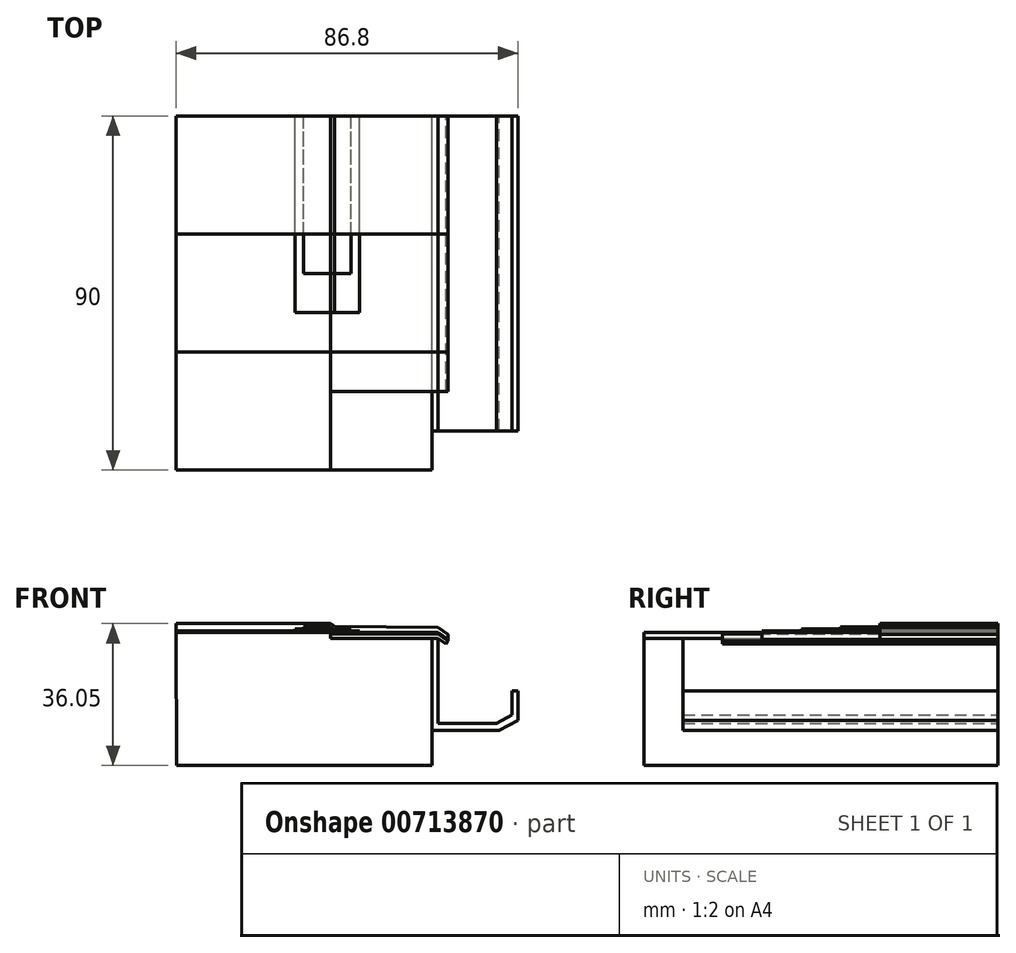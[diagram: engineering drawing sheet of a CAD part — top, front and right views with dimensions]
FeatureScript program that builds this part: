
annotation { "Feature Type Name" : "Feature", "Feature Type Description" : "" }
export const myFeature = defineFeature(function(context is Context, id is Id, definition is map)
    precondition{}
    {
        {
            var Q0;
            Q0=qCreatedBy(makeId("Front.planeOp"),FACE);
            var sketch = newSketch(context, id + "F0", { "sketchPlane" : qUnion([Q0])});
            skLineSegment(sketch, "E0", {"start": v(-75.03, 19.01) * mm, "end": v(-35.84, 19.01) * mm});
            skLineSegment(sketch, "E1", {"start": v(-10, 16.28) * mm, "end": v(-10, -14.78) * mm});
            skLineSegment(sketch, "E2", {"start": v(-10, -14.78) * mm, "end": v(-74.97, -14.78) * mm});
            skLineSegment(sketch, "E3", {"start": v(-74.97, -14.78) * mm, "end": v(-75.03, 19.01) * mm});
            skLineSegment(sketch, "E4", {"start": v(-10, -5.84) * mm, "end": v(7, -5.84) * mm});
            skLineSegment(sketch, "E5", {"start": v(7, -5.84) * mm, "end": v(11.77, -3.36) * mm});
            skLineSegment(sketch, "E6", {"start": v(11.77, -3.36) * mm, "end": v(11.77, 4.25) * mm});
            skLineSegment(sketch, "E7", {"start": v(-35.84, 17.55) * mm, "end": v(-8.56, 17.55) * mm});
            skLineSegment(sketch, "E8", {"start": v(-8.56, 17.55) * mm, "end": v(-8.56, -4.04) * mm});
            skLineSegment(sketch, "E9", {"start": v(-8.56, -4.04) * mm, "end": v(6.35, -4.04) * mm});
            skLineSegment(sketch, "E10", {"start": v(6.35, -4.04) * mm, "end": v(10.35, -1.92) * mm});
            skLineSegment(sketch, "E11", {"start": v(10.35, -1.92) * mm, "end": v(10.35, 4.2) * mm});
            skLineSegment(sketch, "E12", {"start": v(10.35, 4.2) * mm, "end": v(11.77, 4.25) * mm});
            skLineSegment(sketch, "E13", {"start": v(-8.56, 17.55) * mm, "end": v(-6.47, 16.15) * mm});
            skLineSegment(sketch, "E14", {"start": v(-6.47, 16.15) * mm, "end": v(-5.95, 16.94) * mm});
            skLineSegment(sketch, "E15", {"start": v(-5.95, 16.94) * mm, "end": v(-8.56, 18.69) * mm});
            skLineSegment(sketch, "E16", {"start": v(-8.56, 18.69) * mm, "end": v(-35.84, 18.69) * mm});
            skLineSegment(sketch, "E17", {"start": v(-75.03, 19.01) * mm, "end": v(-75.03, 19.4) * mm});
            skLineSegment(sketch, "E18", {"start": v(-75.03, 19.4) * mm, "end": v(-35.84, 19.4) * mm});
            skLineSegment(sketch, "E19", {"start": v(-35.84, 19.4) * mm, "end": v(-35.84, 19.01) * mm});
            skLineSegment(sketch, "E20", {"start": v(-35.84, 19.01) * mm, "end": v(-8.48, 19.01) * mm});
            skLineSegment(sketch, "E21", {"start": v(-8.48, 19.01) * mm, "end": v(-5.95, 17.32) * mm});
            skLineSegment(sketch, "E22", {"start": v(-5.95, 17.32) * mm, "end": v(-5.95, 16.94) * mm});
            skLineSegment(sketch, "E23", {"start": v(-44.83, 19.4) * mm, "end": v(-44.83, 19.98) * mm});
            skLineSegment(sketch, "E24", {"start": v(-44.83, 19.98) * mm, "end": v(-35.84, 19.98) * mm});
            skLineSegment(sketch, "E25", {"start": v(-35.84, 19.98) * mm, "end": v(-34.74, 19.4) * mm});
            skLineSegment(sketch, "E26", {"start": v(-34.74, 19.4) * mm, "end": v(-28.5, 19.4) * mm});
            skLineSegment(sketch, "E27", {"start": v(-28.5, 19.4) * mm, "end": v(-28.5, 19.01) * mm});
            skLineSegment(sketch, "E28", {"start": v(-42.7, 19.98) * mm, "end": v(-42.7, 20.43) * mm});
            skLineSegment(sketch, "E29", {"start": v(-42.7, 20.43) * mm, "end": v(-35.84, 20.43) * mm});
            skLineSegment(sketch, "E30", {"start": v(-35.84, 20.43) * mm, "end": v(-34.79, 19.72) * mm});
            skLineSegment(sketch, "E31", {"start": v(-34.79, 19.72) * mm, "end": v(-30.54, 19.72) * mm});
            skLineSegment(sketch, "E32", {"start": v(-30.54, 19.72) * mm, "end": v(-30.54, 19.4) * mm});
            skLineSegment(sketch, "E33", {"start": v(-75.03, 19.4) * mm, "end": v(-75.03, 21.27) * mm});
            skLineSegment(sketch, "E34", {"start": v(-75.03, 21.27) * mm, "end": v(-35.84, 21.27) * mm});
            skLineSegment(sketch, "E35", {"start": v(-35.84, 21.27) * mm, "end": v(-34.76, 20.54) * mm});
            skLineSegment(sketch, "E36", {"start": v(-34.76, 20.54) * mm, "end": v(-8.48, 20.27) * mm});
            skLineSegment(sketch, "E37", {"start": v(-8.48, 20.27) * mm, "end": v(-5.95, 18.56) * mm});
            skLineSegment(sketch, "E38", {"start": v(-5.95, 18.56) * mm, "end": v(-5.95, 17.32) * mm});
            skLineSegment(sketch, "E39", {"start": v(-10, 16.28) * mm, "end": v(-10, 17.55) * mm});
            skLineSegment(sketch, "E40", {"start": v(-35.84, 18.69) * mm, "end": v(-35.84, 17.55) * mm});
            skLineSegment(sketch, "E41", {"start": v(-35.84, 19.01) * mm, "end": v(-35.84, 18.69) * mm});
            skSolve(sketch);
        }
        {
            var Q0;
            {var subQ4=sQuery(id+"F0.wireOp",EDGE,"E0");Q0=makeQuery(id+"F0.imprint","IMPRINT",FACE,{"disambiguationData":[TD([[makeQuery(id+"F0.imprint","IMPRINT",EDGE,{"derivedFrom":subQ4}),-1.0]])]});}
            extrude(context, id + "F1", {"entities" : qUnion([Q0]), "depth" : 90 * mm});
        }
        {
            var Q0;
            {var subQ1=sQuery(id+"F0.wireOp",EDGE,"X7NthfUY-2YMq-oBzr-Tklb-RvFxg7tLHn6k");Q0=makeQuery(id+"F0.imprint","IMPRINT",FACE,{"disambiguationData":[TD([[makeQuery(id+"F0.imprint","IMPRINT",EDGE,{"derivedFrom":subQ1}),1.0]])]});}
            var Q1;
            {var subQ4=sQuery(id+"F0.wireOp",EDGE,"E4");Q1=makeQuery(id+"F0.imprint","IMPRINT",FACE,{"disambiguationData":[TD([[makeQuery(id+"F0.imprint","IMPRINT",EDGE,{"derivedFrom":subQ4}),1.0]])]});}
            extrude(context, id + "F2", {"entities" : qUnion([Q0, Q1]), "depth" : 80 * mm});
        }
        {
            var Q0;
            {var subQ0=sQuery(id+"F0.wireOp",EDGE,"E7");Q0=makeQuery(id+"F0.imprint","IMPRINT",FACE,{"disambiguationData":[TD([[makeQuery(id+"F0.imprint","IMPRINT",EDGE,{"derivedFrom":subQ0}),1.0]])]});}
            extrude(context, id + "F3", {"entities" : qUnion([Q0]), "depth" : 70 * mm});
        }
        {
            var Q0;
            Q0=makeQuery(id+"F0.imprint","IMPRINT",FACE,{"disambiguationData":[TD([[makeQuery(id+"F0.imprint","IMPRINT",EDGE,{"derivedFrom":sQuery(id+"F0.wireOp",EDGE,"E0")}),1.0]])]});
            extrude(context, id + "F4", {"entities" : qUnion([Q0]), "depth" : 60 * mm});
        }
        {
            var Q0;
            Q0=makeQuery(id+"F0.imprint","IMPRINT",FACE,{"disambiguationData":[TD([[makeQuery(id+"F0.imprint","IMPRINT",EDGE,{"derivedFrom":sQuery(id+"F0.wireOp",EDGE,"E15")}),-1.0]])]});
            extrude(context, id + "F5", {"entities" : qUnion([Q0]), "depth" : 60 * mm});
        }
        {
            var Q0;
            {var subQ1=sQuery(id+"F0.wireOp",EDGE,"E19");Q0=makeQuery(id+"F0.imprint","IMPRINT",FACE,{"disambiguationData":[TD([[makeQuery(id+"F0.imprint","IMPRINT",EDGE,{"derivedFrom":subQ1}),1.0]])]});}
            extrude(context, id + "F6", {"entities" : qUnion([Q0]), "depth" : 50 * mm});
        }
        {
            var Q0;
            {var subQ1=sQuery(id+"F0.wireOp",EDGE,"E25");Q0=makeQuery(id+"F0.imprint","IMPRINT",FACE,{"disambiguationData":[TD([[makeQuery(id+"F0.imprint","IMPRINT",EDGE,{"derivedFrom":subQ1}),1.0]])]});}
            extrude(context, id + "F7", {"entities" : qUnion([Q0]), "depth" : 40 * mm});
        }
        {
            var Q0;
            {var subQ8=sQuery(id+"F0.wireOp",EDGE,"E21");Q0=makeQuery(id+"F0.imprint","IMPRINT",FACE,{"disambiguationData":[TD([[makeQuery(id+"F0.imprint","IMPRINT",EDGE,{"derivedFrom":subQ8}),1.0]])]});}
            extrude(context, id + "F8", {"entities" : qUnion([Q0]), "depth" : 30 * mm});
        }
    });
